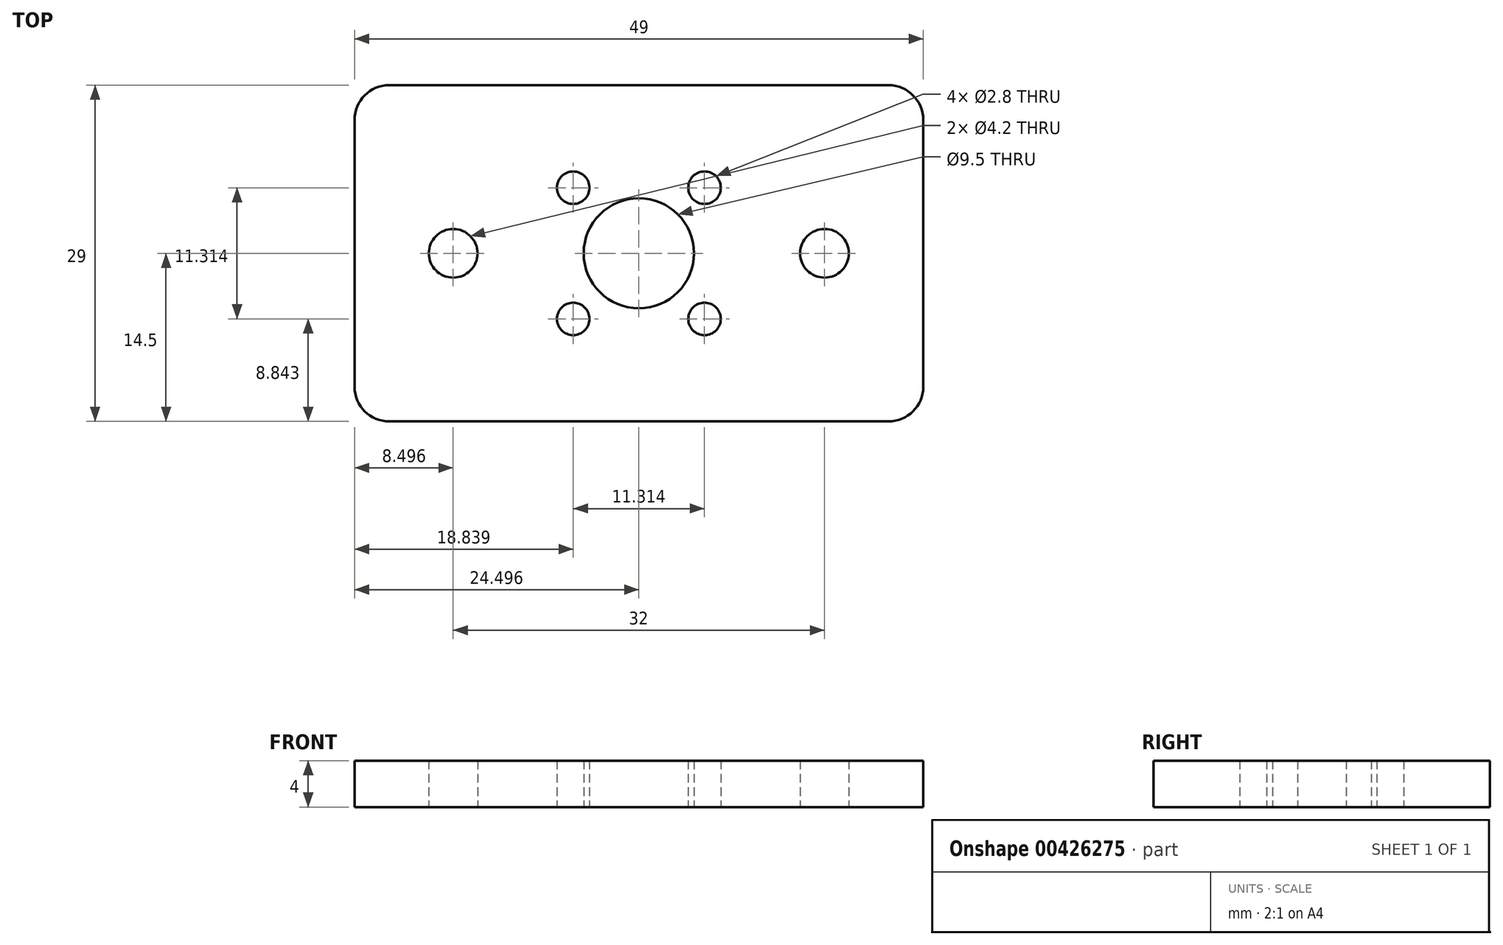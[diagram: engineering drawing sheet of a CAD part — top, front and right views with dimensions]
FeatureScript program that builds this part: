
annotation { "Feature Type Name" : "Feature", "Feature Type Description" : "" }
export const myFeature = defineFeature(function(context is Context, id is Id, definition is map)
    precondition{}
    {
        {
            var Q0;
            Q0=qCreatedBy(makeId("Top.planeOp"),FACE);
            var sketch = newSketch(context, id + "F0", { "sketchPlane" : qUnion([Q0])});
            skLineSegment(sketch, "E0.bottom", {"start": v(-66.68, 40.15) * mm, "end": v(-17.68, 40.15) * mm});
            skLineSegment(sketch, "E0.top", {"start": v(-66.68, 11.15) * mm, "end": v(-17.68, 11.15) * mm});
            skLineSegment(sketch, "E0.left", {"start": v(-66.68, 40.15) * mm, "end": v(-66.68, 11.15) * mm});
            skLineSegment(sketch, "E0.right", {"start": v(-17.68, 40.15) * mm, "end": v(-17.68, 11.15) * mm});
            skCircle(sketch, "E1", {"center": v(-58.18, 25.65) * mm, "radius": 2.1 * mm});
            skPoint(sketch, "E1.centerSnap0", {"position": v(-66.68, 25.65) * mm});
            skCircle(sketch, "E2", {"center": v(-26.18, 25.65) * mm, "radius": 2.1 * mm});
            skCircle(sketch, "E3", {"center": v(-42.18, 25.65) * mm, "radius": 4.75 * mm});
            skPoint(sketch, "E3.centerSnap0", {"position": v(-42.18, 40.15) * mm});
            skCircle(sketch, "E4", {"center": v(-47.84, 31.3) * mm, "radius": 1.4 * mm});
            skCircle(sketch, "E5", {"center": v(-36.53, 31.3) * mm, "radius": 1.4 * mm});
            skCircle(sketch, "E6", {"center": v(-47.84, 20) * mm, "radius": 1.4 * mm});
            skCircle(sketch, "E7", {"center": v(-36.53, 20) * mm, "radius": 1.4 * mm});
            skSolve(sketch);
        }
        {
            var Q0;
            Q0=makeQuery(id+"F0.imprint","IMPRINT",FACE,{"disambiguationData":[TD([[makeQuery(id+"F0.imprint","IMPRINT",EDGE,{"derivedFrom":sQuery(id+"F0.wireOp",EDGE,"E0.bottom")}),-1.0]])]});
            extrude(context, id + "F1", {"entities" : qUnion([Q0]), "depth" : 4 * mm, "offsetDistance" : 25 * mm});
        }
        {
            var Q0;
            Q0=makeQuery(id+"F1.opExtrude","SWEPT_EDGE",EDGE,{"disambiguationData":[OSD([sQuery(id+"F0.wireOp",EDGE,"E0.top"),sQuery(id+"F0.wireOp",EDGE,"E0.left")])]});
            var Q1;
            Q1=makeQuery(id+"F1.opExtrude","SWEPT_EDGE",EDGE,{"disambiguationData":[OSD([sQuery(id+"F0.wireOp",EDGE,"E0.top"),sQuery(id+"F0.wireOp",EDGE,"E0.right")])]});
            var Q2;
            Q2=makeQuery(id+"F1.opExtrude","SWEPT_EDGE",EDGE,{"disambiguationData":[OSD([sQuery(id+"F0.wireOp",EDGE,"E0.bottom"),sQuery(id+"F0.wireOp",EDGE,"E0.right")])]});
            var Q3;
            Q3=makeQuery(id+"F1.opExtrude","SWEPT_EDGE",EDGE,{"disambiguationData":[OSD([sQuery(id+"F0.wireOp",EDGE,"E0.bottom"),sQuery(id+"F0.wireOp",EDGE,"E0.left")])]});
            fillet(context, id + "F2", {"entities" : qUnion([Q0, Q1, Q2, Q3]), "radius" : 3 * mm, "tangentPropagation" : true, "allowEdgeOverflow" : false});
        }
    });
